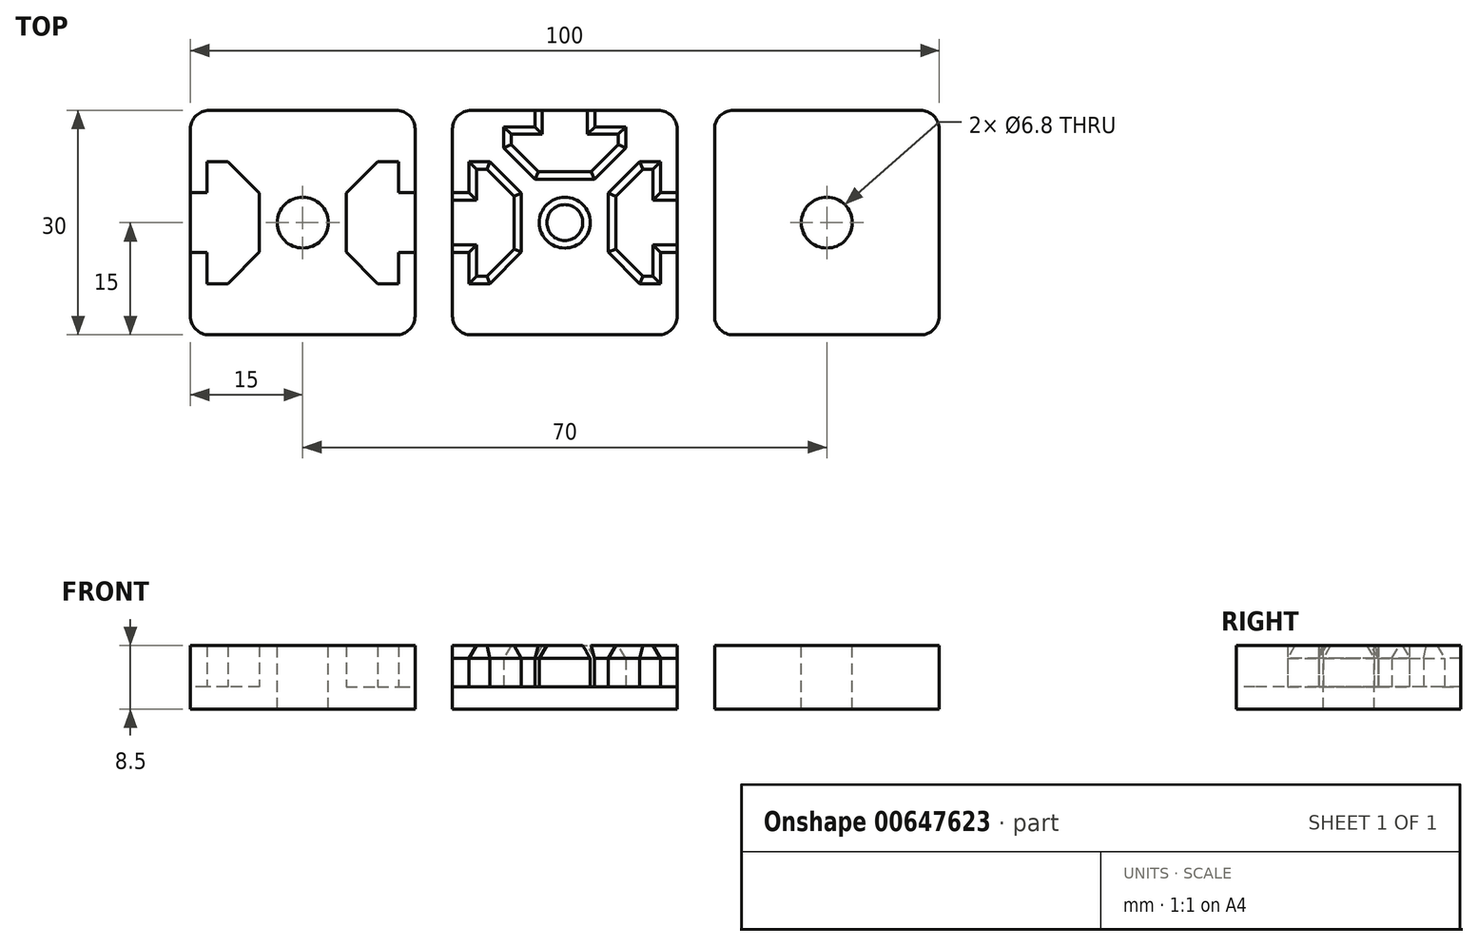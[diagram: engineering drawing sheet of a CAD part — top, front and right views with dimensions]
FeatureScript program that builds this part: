
annotation { "Feature Type Name" : "Feature", "Feature Type Description" : "" }
export const myFeature = defineFeature(function(context is Context, id is Id, definition is map)
    precondition{}
    {
        {
            var Q0;
            Q0=qCreatedBy(makeId("Top.planeOp"),FACE);
            var sketch = newSketch(context, id + "F0", { "sketchPlane" : qUnion([Q0])});
            skLineSegment(sketch, "E0.bottom", {"start": v(-12.5, 15) * mm, "end": v(12.5, 15) * mm});
            skLineSegment(sketch, "E0.top", {"start": v(-12.5, -15) * mm, "end": v(12.5, -15) * mm});
            skLineSegment(sketch, "E0.left", {"start": v(-15, 12.5) * mm, "end": v(-15, -12.5) * mm});
            skLineSegment(sketch, "E0.right", {"start": v(15, 12.5) * mm, "end": v(15, -12.5) * mm});
            skPoint(sketch, "E0.middle", {"position": v(0, 0) * mm});
            skPoint(sketch, "E1.visualSharp", {"position": v(-15, 15) * mm});
            skArc(sketch, "E1.filletArc", {"start": v(-12.5, 15) * mm, "mid": v(-14.27, 14.27) * mm, "end": v(-15, 12.5) * mm});
            skPoint(sketch, "E2.visualSharp", {"position": v(-15, -15) * mm});
            skArc(sketch, "E2.filletArc", {"start": v(-15, -12.5) * mm, "mid": v(-14.27, -14.27) * mm, "end": v(-12.5, -15) * mm});
            skPoint(sketch, "E3.visualSharp", {"position": v(15, -15) * mm});
            skArc(sketch, "E3.filletArc", {"start": v(12.5, -15) * mm, "mid": v(14.27, -14.27) * mm, "end": v(15, -12.5) * mm});
            skPoint(sketch, "E4.visualSharp", {"position": v(15, 15) * mm});
            skArc(sketch, "E4.filletArc", {"start": v(15, 12.5) * mm, "mid": v(14.27, 14.27) * mm, "end": v(12.5, 15) * mm});
            skLineSegment(sketch, "E5", {"start": v(-15, 15) * mm, "end": v(15, -15) * mm, "construction": true});
            skLineSegment(sketch, "E6", {"start": v(15, 15) * mm, "end": v(-15, -15) * mm, "construction": true});
            skLineSegment(sketch, "E7", {"start": v(15, 4) * mm, "end": v(12.8, 4) * mm});
            skLineSegment(sketch, "E8", {"start": v(12.8, 4) * mm, "end": v(12.8, 8.15) * mm});
            skLineSegment(sketch, "E9", {"start": v(12.8, 8.15) * mm, "end": v(10, 8.15) * mm});
            skLineSegment(sketch, "E10", {"start": v(10, 8.15) * mm, "end": v(5.8, 3.95) * mm});
            skLineSegment(sketch, "E11", {"start": v(5.8, 3.95) * mm, "end": v(5.8, -3.95) * mm});
            skLineSegment(sketch, "E12", {"start": v(5.8, -3.95) * mm, "end": v(10, -8.15) * mm});
            skLineSegment(sketch, "E13", {"start": v(10, -8.15) * mm, "end": v(12.8, -8.15) * mm});
            skLineSegment(sketch, "E14", {"start": v(12.8, -8.15) * mm, "end": v(12.8, -4) * mm});
            skLineSegment(sketch, "E15", {"start": v(12.8, -4) * mm, "end": v(15, -4) * mm});
            skPoint(sketch, "E16", {"position": v(5.8, 0) * mm});
            skLineSegment(sketch, "E17", {"start": v(12.8, 4) * mm, "end": v(12.8, -4) * mm, "construction": true});
            skPoint(sketch, "E18", {"position": v(12.8, 0) * mm});
            skLineSegment(sketch, "E19.MirrorCS", {"start": v(8.15, 10) * mm, "end": v(3.95, 5.8) * mm});
            skLineSegment(sketch, "E20.MirrorCS", {"start": v(8.15, 12.8) * mm, "end": v(8.15, 10) * mm});
            skLineSegment(sketch, "E21.MirrorCS", {"start": v(4, 12.8) * mm, "end": v(8.15, 12.8) * mm});
            skLineSegment(sketch, "E22.MirrorCS", {"start": v(4, 15) * mm, "end": v(4, 12.8) * mm});
            skLineSegment(sketch, "E23.MirrorCS", {"start": v(-4, 12.8) * mm, "end": v(-4, 15) * mm});
            skLineSegment(sketch, "E24.MirrorCS", {"start": v(-8.15, 12.8) * mm, "end": v(-4, 12.8) * mm});
            skLineSegment(sketch, "E25.MirrorCS", {"start": v(-8.15, 10) * mm, "end": v(-8.15, 12.8) * mm});
            skLineSegment(sketch, "E26.MirrorCS", {"start": v(-3.95, 5.8) * mm, "end": v(-8.15, 10) * mm});
            skLineSegment(sketch, "E27.MirrorCS", {"start": v(3.95, 5.8) * mm, "end": v(-3.95, 5.8) * mm});
            skLineSegment(sketch, "E28.MirrorCS", {"start": v(-5.8, -3.95) * mm, "end": v(-5.8, 3.95) * mm});
            skLineSegment(sketch, "E29.MirrorCS", {"start": v(-10, -8.15) * mm, "end": v(-5.8, -3.95) * mm});
            skLineSegment(sketch, "E30.MirrorCS", {"start": v(-12.8, -8.15) * mm, "end": v(-10, -8.15) * mm});
            skLineSegment(sketch, "E31.MirrorCS", {"start": v(-12.8, -4) * mm, "end": v(-12.8, -8.15) * mm});
            skLineSegment(sketch, "E32.MirrorCS", {"start": v(-15, -4) * mm, "end": v(-12.8, -4) * mm});
            skLineSegment(sketch, "E33.MirrorCS", {"start": v(-12.8, 4) * mm, "end": v(-15, 4) * mm});
            skLineSegment(sketch, "E34.MirrorCS", {"start": v(-12.8, 8.15) * mm, "end": v(-12.8, 4) * mm});
            skLineSegment(sketch, "E35.MirrorCS", {"start": v(-10, 8.15) * mm, "end": v(-12.8, 8.15) * mm});
            skLineSegment(sketch, "E36.MirrorCS", {"start": v(-5.8, 3.95) * mm, "end": v(-10, 8.15) * mm});
            skLineSegment(sketch, "E37.MirrorCS", {"start": v(-3.95, -5.8) * mm, "end": v(3.95, -5.8) * mm});
            skLineSegment(sketch, "E38.MirrorCS", {"start": v(-8.15, -10) * mm, "end": v(-3.95, -5.8) * mm});
            skLineSegment(sketch, "E39.MirrorCS", {"start": v(-8.15, -12.8) * mm, "end": v(-8.15, -10) * mm});
            skLineSegment(sketch, "E40.MirrorCS", {"start": v(-4, -12.8) * mm, "end": v(-8.15, -12.8) * mm});
            skLineSegment(sketch, "E41.MirrorCS", {"start": v(-4, -15) * mm, "end": v(-4, -12.8) * mm});
            skLineSegment(sketch, "E42.MirrorCS", {"start": v(4, -12.8) * mm, "end": v(4, -15) * mm});
            skLineSegment(sketch, "E43.MirrorCS", {"start": v(8.15, -12.8) * mm, "end": v(4, -12.8) * mm});
            skLineSegment(sketch, "E44.MirrorCS", {"start": v(8.15, -10) * mm, "end": v(8.15, -12.8) * mm});
            skLineSegment(sketch, "E45.MirrorCS", {"start": v(3.95, -5.8) * mm, "end": v(8.15, -10) * mm});
            skLineSegment(sketch, "E46", {"start": v(-17.5, 20.45) * mm, "end": v(-17.5, -22.2) * mm, "construction": true});
            skLineSegment(sketch, "E47", {"start": v(17.5, 19.31) * mm, "end": v(17.5, -20.78) * mm, "construction": true});
            skArc(sketch, "E48.MirrorCS", {"start": v(-22.5, 15) * mm, "mid": v(-20.73, 14.27) * mm, "end": v(-20, 12.5) * mm});
            skArc(sketch, "E49.MirrorCS", {"start": v(-20, -12.5) * mm, "mid": v(-20.73, -14.27) * mm, "end": v(-22.5, -15) * mm});
            skLineSegment(sketch, "E50.MirrorCS", {"start": v(-39, -12.8) * mm, "end": v(-39, -15) * mm});
            skLineSegment(sketch, "E51.MirrorCS", {"start": v(-39, 15) * mm, "end": v(-39, 12.8) * mm});
            skArc(sketch, "E52.MirrorCS", {"start": v(-47.5, -15) * mm, "mid": v(-49.27, -14.27) * mm, "end": v(-50, -12.5) * mm});
            skArc(sketch, "E53.MirrorCS", {"start": v(-50, 12.5) * mm, "mid": v(-49.27, 14.27) * mm, "end": v(-47.5, 15) * mm});
            skLineSegment(sketch, "E54.MirrorCS", {"start": v(-20, -4) * mm, "end": v(-22.2, -4) * mm});
            skLineSegment(sketch, "E55.MirrorCS", {"start": v(-31, 12.8) * mm, "end": v(-31, 15) * mm});
            skLineSegment(sketch, "E56.MirrorCS", {"start": v(-22.2, 4) * mm, "end": v(-20, 4) * mm});
            skLineSegment(sketch, "E57.MirrorCS", {"start": v(-31, -15) * mm, "end": v(-31, -12.8) * mm});
            skLineSegment(sketch, "E58.MirrorCS", {"start": v(-22.2, 8.15) * mm, "end": v(-22.2, 4) * mm});
            skLineSegment(sketch, "E59.MirrorCS", {"start": v(-47.8, 4) * mm, "end": v(-47.8, -4) * mm, "construction": true});
            skLineSegment(sketch, "E60.MirrorCS", {"start": v(-45, 8.15) * mm, "end": v(-40.8, 3.95) * mm});
            skLineSegment(sketch, "E61.MirrorCS", {"start": v(-43.15, -10) * mm, "end": v(-43.15, -12.8) * mm});
            skLineSegment(sketch, "E62.MirrorCS", {"start": v(-25, 8.15) * mm, "end": v(-22.2, 8.15) * mm});
            skLineSegment(sketch, "E63.MirrorCS", {"start": v(-29.2, -3.95) * mm, "end": v(-29.2, 3.95) * mm});
            skLineSegment(sketch, "E64.MirrorCS", {"start": v(-43.15, 10) * mm, "end": v(-38.95, 5.8) * mm});
            skLineSegment(sketch, "E65.MirrorCS", {"start": v(-50, 12.5) * mm, "end": v(-50, -12.5) * mm});
            skPoint(sketch, "E66.MirrorP", {"position": v(-20, -15) * mm});
            skLineSegment(sketch, "E67.MirrorCS", {"start": v(-43.15, -12.8) * mm, "end": v(-39, -12.8) * mm});
            skLineSegment(sketch, "E68.MirrorCS", {"start": v(-38.95, 5.8) * mm, "end": v(-31.05, 5.8) * mm});
            skLineSegment(sketch, "E69.MirrorCS", {"start": v(-38.95, -5.8) * mm, "end": v(-43.15, -10) * mm});
            skLineSegment(sketch, "E70.MirrorCS", {"start": v(-25, -8.15) * mm, "end": v(-29.2, -3.95) * mm});
            skLineSegment(sketch, "E71.MirrorCS", {"start": v(-29.2, 3.95) * mm, "end": v(-25, 8.15) * mm});
            skLineSegment(sketch, "E72.MirrorCS", {"start": v(-43.15, 12.8) * mm, "end": v(-43.15, 10) * mm});
            skLineSegment(sketch, "E73.MirrorCS", {"start": v(-26.85, 12.8) * mm, "end": v(-31, 12.8) * mm});
            skLineSegment(sketch, "E74.MirrorCS", {"start": v(-22.2, -8.15) * mm, "end": v(-25, -8.15) * mm});
            skPoint(sketch, "E75.MirrorP", {"position": v(-50, -15) * mm});
            skLineSegment(sketch, "E76.MirrorCS", {"start": v(-31.05, 5.8) * mm, "end": v(-26.85, 10) * mm});
            skLineSegment(sketch, "E77.MirrorCS", {"start": v(-26.85, -10) * mm, "end": v(-31.05, -5.8) * mm});
            skLineSegment(sketch, "E78.MirrorCS", {"start": v(-40.8, 3.95) * mm, "end": v(-40.8, -3.95) * mm});
            skLineSegment(sketch, "E79.MirrorCS", {"start": v(-40.8, -3.95) * mm, "end": v(-45, -8.15) * mm});
            skLineSegment(sketch, "E80.MirrorCS", {"start": v(-22.5, 15) * mm, "end": v(-47.5, 15) * mm});
            skLineSegment(sketch, "E81.MirrorCS", {"start": v(-22.5, -15) * mm, "end": v(-47.5, -15) * mm});
            skLineSegment(sketch, "E82.MirrorCS", {"start": v(-20, 12.5) * mm, "end": v(-20, -12.5) * mm});
            skPoint(sketch, "E83.MirrorP", {"position": v(-40.8, 0) * mm});
            skLineSegment(sketch, "E84.MirrorCS", {"start": v(-22.2, -4) * mm, "end": v(-22.2, -8.15) * mm});
            skLineSegment(sketch, "E85.MirrorCS", {"start": v(-45, -8.15) * mm, "end": v(-47.8, -8.15) * mm});
            skPoint(sketch, "E86.MirrorP", {"position": v(-47.8, 0) * mm});
            skLineSegment(sketch, "E87.MirrorCS", {"start": v(-47.8, -8.15) * mm, "end": v(-47.8, -4) * mm});
            skLineSegment(sketch, "E88.MirrorCS", {"start": v(-31, -12.8) * mm, "end": v(-26.85, -12.8) * mm});
            skLineSegment(sketch, "E89.MirrorCS", {"start": v(-20, 15) * mm, "end": v(-50, -15) * mm, "construction": true});
            skPoint(sketch, "E90.MirrorP", {"position": v(-20, 15) * mm});
            skLineSegment(sketch, "E91.MirrorCS", {"start": v(-26.85, -12.8) * mm, "end": v(-26.85, -10) * mm});
            skLineSegment(sketch, "E92.MirrorCS", {"start": v(-47.8, 4) * mm, "end": v(-47.8, 8.15) * mm});
            skLineSegment(sketch, "E93.MirrorCS", {"start": v(-47.8, 8.15) * mm, "end": v(-45, 8.15) * mm});
            skLineSegment(sketch, "E94.MirrorCS", {"start": v(-50, 15) * mm, "end": v(-20, -15) * mm, "construction": true});
            skPoint(sketch, "E95.MirrorP", {"position": v(-35, 0) * mm});
            skLineSegment(sketch, "E96.MirrorCS", {"start": v(-47.8, -4) * mm, "end": v(-50, -4) * mm});
            skLineSegment(sketch, "E97.MirrorCS", {"start": v(-26.85, 10) * mm, "end": v(-26.85, 12.8) * mm});
            skPoint(sketch, "E98.MirrorP", {"position": v(-50, 15) * mm});
            skLineSegment(sketch, "E99.MirrorCS", {"start": v(-31.05, -5.8) * mm, "end": v(-38.95, -5.8) * mm});
            skLineSegment(sketch, "E100.MirrorCS", {"start": v(-39, 12.8) * mm, "end": v(-43.15, 12.8) * mm});
            skLineSegment(sketch, "E101.MirrorCS", {"start": v(-50, 4) * mm, "end": v(-47.8, 4) * mm});
            skArc(sketch, "E102.MirrorCS", {"start": v(50, -12.5) * mm, "mid": v(49.27, -14.27) * mm, "end": v(47.5, -15) * mm});
            skLineSegment(sketch, "E103.MirrorCS", {"start": v(39, -15) * mm, "end": v(39, -12.8) * mm});
            skArc(sketch, "E104.MirrorCS", {"start": v(20, 12.5) * mm, "mid": v(20.73, 14.27) * mm, "end": v(22.5, 15) * mm});
            skArc(sketch, "E105.MirrorCS", {"start": v(22.5, -15) * mm, "mid": v(20.73, -14.27) * mm, "end": v(20, -12.5) * mm});
            skArc(sketch, "E106.MirrorCS", {"start": v(47.5, 15) * mm, "mid": v(49.27, 14.27) * mm, "end": v(50, 12.5) * mm});
            skLineSegment(sketch, "E107.MirrorCS", {"start": v(47.8, 4) * mm, "end": v(50, 4) * mm});
            skLineSegment(sketch, "E108.MirrorCS", {"start": v(31, -12.8) * mm, "end": v(31, -15) * mm});
            skLineSegment(sketch, "E109.MirrorCS", {"start": v(50, -4) * mm, "end": v(47.8, -4) * mm});
            skLineSegment(sketch, "E110.MirrorCS", {"start": v(22.2, -4) * mm, "end": v(20, -4) * mm});
            skLineSegment(sketch, "E111.MirrorCS", {"start": v(39, -12.8) * mm, "end": v(43.15, -12.8) * mm});
            skLineSegment(sketch, "E112.MirrorCS", {"start": v(22.2, -8.15) * mm, "end": v(22.2, -4) * mm});
            skLineSegment(sketch, "E113.MirrorCS", {"start": v(39, 12.8) * mm, "end": v(39, 15) * mm});
            skLineSegment(sketch, "E114.MirrorCS", {"start": v(31, 12.8) * mm, "end": v(26.85, 12.8) * mm});
            skLineSegment(sketch, "E115.MirrorCS", {"start": v(38.95, -5.8) * mm, "end": v(31.05, -5.8) * mm});
            skLineSegment(sketch, "E116.MirrorCS", {"start": v(47.8, -8.15) * mm, "end": v(45, -8.15) * mm});
            skLineSegment(sketch, "E117.MirrorCS", {"start": v(26.85, 12.8) * mm, "end": v(26.85, 10) * mm});
            skLineSegment(sketch, "E118.MirrorCS", {"start": v(40.8, 3.95) * mm, "end": v(45, 8.15) * mm});
            skLineSegment(sketch, "E119.MirrorCS", {"start": v(45, -8.15) * mm, "end": v(40.8, -3.95) * mm});
            skLineSegment(sketch, "E120.MirrorCS", {"start": v(31.05, -5.8) * mm, "end": v(26.85, -10) * mm});
            skLineSegment(sketch, "E121.MirrorCS", {"start": v(31.05, 5.8) * mm, "end": v(38.95, 5.8) * mm});
            skPoint(sketch, "E122.MirrorP", {"position": v(20, -15) * mm});
            skLineSegment(sketch, "E123.MirrorCS", {"start": v(26.85, -12.8) * mm, "end": v(31, -12.8) * mm});
            skLineSegment(sketch, "E124.MirrorCS", {"start": v(26.85, 10) * mm, "end": v(31.05, 5.8) * mm});
            skLineSegment(sketch, "E125.MirrorCS", {"start": v(45, 8.15) * mm, "end": v(47.8, 8.15) * mm});
            skLineSegment(sketch, "E126.MirrorCS", {"start": v(40.8, -3.95) * mm, "end": v(40.8, 3.95) * mm});
            skLineSegment(sketch, "E127.MirrorCS", {"start": v(26.85, -10) * mm, "end": v(26.85, -12.8) * mm});
            skLineSegment(sketch, "E128.MirrorCS", {"start": v(20, 12.5) * mm, "end": v(20, -12.5) * mm});
            skLineSegment(sketch, "E129.MirrorCS", {"start": v(43.15, 10) * mm, "end": v(43.15, 12.8) * mm});
            skPoint(sketch, "E130.MirrorP", {"position": v(50, 15) * mm});
            skLineSegment(sketch, "E131.MirrorCS", {"start": v(47.8, 8.15) * mm, "end": v(47.8, 4) * mm});
            skLineSegment(sketch, "E132.MirrorCS", {"start": v(29.2, 3.95) * mm, "end": v(29.2, -3.95) * mm});
            skPoint(sketch, "E133.MirrorP", {"position": v(50, -15) * mm});
            skLineSegment(sketch, "E134.MirrorCS", {"start": v(43.15, -10) * mm, "end": v(38.95, -5.8) * mm});
            skLineSegment(sketch, "E135.MirrorCS", {"start": v(20, 15) * mm, "end": v(50, -15) * mm, "construction": true});
            skLineSegment(sketch, "E136.MirrorCS", {"start": v(43.15, 12.8) * mm, "end": v(39, 12.8) * mm});
            skLineSegment(sketch, "E137.MirrorCS", {"start": v(29.2, -3.95) * mm, "end": v(25, -8.15) * mm});
            skPoint(sketch, "E138.MirrorP", {"position": v(29.2, 0) * mm});
            skLineSegment(sketch, "E139.MirrorCS", {"start": v(25, -8.15) * mm, "end": v(22.2, -8.15) * mm});
            skLineSegment(sketch, "E140.MirrorCS", {"start": v(38.95, 5.8) * mm, "end": v(43.15, 10) * mm});
            skLineSegment(sketch, "E141.MirrorCS", {"start": v(43.15, -12.8) * mm, "end": v(43.15, -10) * mm});
            skPoint(sketch, "E142.MirrorP", {"position": v(35, 0) * mm});
            skPoint(sketch, "E143.MirrorP", {"position": v(22.2, 0) * mm});
            skPoint(sketch, "E144.MirrorP", {"position": v(20, 15) * mm});
            skLineSegment(sketch, "E145.MirrorCS", {"start": v(22.2, 8.15) * mm, "end": v(25, 8.15) * mm});
            skLineSegment(sketch, "E146.MirrorCS", {"start": v(20, 4) * mm, "end": v(22.2, 4) * mm});
            skLineSegment(sketch, "E147.MirrorCS", {"start": v(22.2, 4) * mm, "end": v(22.2, 8.15) * mm});
            skLineSegment(sketch, "E148.MirrorCS", {"start": v(31, 15) * mm, "end": v(31, 12.8) * mm});
            skLineSegment(sketch, "E149.MirrorCS", {"start": v(50, 15) * mm, "end": v(20, -15) * mm, "construction": true});
            skLineSegment(sketch, "E150.MirrorCS", {"start": v(47.8, -4) * mm, "end": v(47.8, -8.15) * mm});
            skLineSegment(sketch, "E151.MirrorCS", {"start": v(22.2, 4) * mm, "end": v(22.2, -4) * mm, "construction": true});
            skLineSegment(sketch, "E152.MirrorCS", {"start": v(47.5, -15) * mm, "end": v(22.5, -15) * mm});
            skLineSegment(sketch, "E153.MirrorCS", {"start": v(47.5, 15) * mm, "end": v(22.5, 15) * mm});
            skLineSegment(sketch, "E154.MirrorCS", {"start": v(25, 8.15) * mm, "end": v(29.2, 3.95) * mm});
            skLineSegment(sketch, "E155.MirrorCS", {"start": v(50, 12.5) * mm, "end": v(50, -12.5) * mm});
            skCircle(sketch, "E156", {"center": v(0, 0) * mm, "radius": 3.4 * mm});
            skCircle(sketch, "E157.MirrorC", {"center": v(-35, 0) * mm, "radius": 3.4 * mm});
            skCircle(sketch, "E158.MirrorC", {"center": v(35, 0) * mm, "radius": 3.4 * mm});
            skSolve(sketch);
        }
        {
            var Q0;
            Q0=makeQuery(id+"F0.imprint","IMPRINT",FACE,{"disambiguationData":[TD([[makeQuery(id+"F0.imprint","IMPRINT",EDGE,{"derivedFrom":sQuery(id+"F0.wireOp",EDGE,"E0.bottom")}),-1.0]])]});
            var Q1;
            {var subQ0=sQuery(id+"F0.wireOp",EDGE,"E7");Q1=makeQuery(id+"F0.imprint","IMPRINT",FACE,{"disambiguationData":[TD([[makeQuery(id+"F0.imprint","IMPRINT",EDGE,{"derivedFrom":subQ0}),1.0]])]});}
            var Q2;
            Q2=makeQuery(id+"F0.imprint","IMPRINT",FACE,{"disambiguationData":[TD([[makeQuery(id+"F0.imprint","IMPRINT",EDGE,{"derivedFrom":sQuery(id+"F0.wireOp",EDGE,"E28.MirrorCS")}),1.0]])]});
            var Q3;
            Q3=makeQuery(id+"F0.imprint","IMPRINT",FACE,{"disambiguationData":[TD([[makeQuery(id+"F0.imprint","IMPRINT",EDGE,{"derivedFrom":sQuery(id+"F0.wireOp",EDGE,"E37.MirrorCS")}),-1.0]])]});
            var Q4;
            Q4=makeQuery(id+"F0.imprint","IMPRINT",FACE,{"disambiguationData":[TD([[makeQuery(id+"F0.imprint","IMPRINT",EDGE,{"derivedFrom":sQuery(id+"F0.wireOp",EDGE,"E19.MirrorCS")}),-1.0]])]});
            var Q5;
            Q5=makeQuery(id+"F0.imprint","IMPRINT",FACE,{"disambiguationData":[TD([[makeQuery(id+"F0.imprint","IMPRINT",EDGE,{"derivedFrom":sQuery(id+"F0.wireOp",EDGE,"E156")}),1.0]])]});
            extrude(context, id + "F1", {"entities" : qUnion([Q0, Q1, Q2, Q3, Q4, Q5]), "oppositeDirection" : true, "depth" : 3 * mm, "offsetDistance" : 25 * mm});
        }
        {
            var Q0;
            Q0=makeQuery(id+"F0.imprint","IMPRINT",FACE,{"disambiguationData":[TD([[makeQuery(id+"F0.imprint","IMPRINT",EDGE,{"derivedFrom":sQuery(id+"F0.wireOp",EDGE,"E28.MirrorCS")}),1.0]])]});
            var Q1;
            Q1=makeQuery(id+"F0.imprint","IMPRINT",FACE,{"disambiguationData":[TD([[makeQuery(id+"F0.imprint","IMPRINT",EDGE,{"derivedFrom":sQuery(id+"F0.wireOp",EDGE,"E19.MirrorCS")}),-1.0]])]});
            var Q2;
            {var subQ0=sQuery(id+"F0.wireOp",EDGE,"E7");Q2=makeQuery(id+"F0.imprint","IMPRINT",FACE,{"disambiguationData":[TD([[makeQuery(id+"F0.imprint","IMPRINT",EDGE,{"derivedFrom":subQ0}),1.0]])]});}
            var Q3;
            Q3=makeQuery(id+"F0.imprint","IMPRINT",FACE,{"disambiguationData":[TD([[makeQuery(id+"F0.imprint","IMPRINT",EDGE,{"derivedFrom":sQuery(id+"F0.wireOp",EDGE,"E156")}),1.0]])]});
            extrude(context, id + "F2", {"entities" : qUnion([Q0, Q1, Q2, Q3]), "operationType" : NewBodyOperationType.ADD, "depth" : 5.5 * mm, "offsetDistance" : 25 * mm});
        }
        {
            var Q0;
            {var subQ3=sQuery(id+"F0.wireOp",EDGE,"E48.MirrorCS");Q0=makeQuery(id+"F0.imprint","IMPRINT",FACE,{"disambiguationData":[TD([[makeQuery(id+"F0.imprint","IMPRINT",EDGE,{"derivedFrom":subQ3}),-1.0]])]});}
            var Q1;
            {var subQ1=sQuery(id+"F0.wireOp",EDGE,"E50.MirrorCS");Q1=makeQuery(id+"F0.imprint","IMPRINT",FACE,{"disambiguationData":[TD([[makeQuery(id+"F0.imprint","IMPRINT",EDGE,{"derivedFrom":subQ1}),1.0]])]});}
            var Q2;
            {var subQ1=sQuery(id+"F0.wireOp",EDGE,"E54.MirrorCS");Q2=makeQuery(id+"F0.imprint","IMPRINT",FACE,{"disambiguationData":[TD([[makeQuery(id+"F0.imprint","IMPRINT",EDGE,{"derivedFrom":subQ1}),-1.0]])]});}
            var Q3;
            {var subQ1=sQuery(id+"F0.wireOp",EDGE,"E51.MirrorCS");Q3=makeQuery(id+"F0.imprint","IMPRINT",FACE,{"disambiguationData":[TD([[makeQuery(id+"F0.imprint","IMPRINT",EDGE,{"derivedFrom":subQ1}),1.0]])]});}
            var Q4;
            Q4=makeQuery(id+"F0.imprint","IMPRINT",FACE,{"disambiguationData":[TD([[makeQuery(id+"F0.imprint","IMPRINT",EDGE,{"derivedFrom":sQuery(id+"F0.wireOp",EDGE,"E60.MirrorCS")}),-1.0]])]});
            var Q5;
            Q5=makeQuery(id+"F0.imprint","IMPRINT",FACE,{"disambiguationData":[TD([[makeQuery(id+"F0.imprint","IMPRINT",EDGE,{"derivedFrom":sQuery(id+"F0.wireOp",EDGE,"E157.MirrorC")}),-1.0]])]});
            var Q6;
            Q6=makeQuery(id+"F1.opExtrude","CAP_FACE",FACE,{"disambiguationData":[OSD([sQuery(id+"F0.wireOp",EDGE,"E0.bottom"),sQuery(id+"F0.wireOp",EDGE,"E0.top"),sQuery(id+"F0.wireOp",EDGE,"E0.left"),sQuery(id+"F0.wireOp",EDGE,"E0.right"),sQuery(id+"F0.wireOp",EDGE,"E1.filletArc"),sQuery(id+"F0.wireOp",EDGE,"E2.filletArc"),sQuery(id+"F0.wireOp",EDGE,"E3.filletArc"),sQuery(id+"F0.wireOp",EDGE,"E4.filletArc")])],"isStart":false});
            extrude(context, id + "F3", {"entities" : qUnion([Q0, Q1, Q2, Q3, Q4, Q5]), "endBound" : BoundingType.UP_TO_SURFACE, "oppositeDirection" : true, "depth" : 5 * mm, "endBoundEntityFace" : qUnion([Q6]), "offsetDistance" : 25 * mm});
        }
        {
            var Q0;
            {var subQ1=sQuery(id+"F0.wireOp",EDGE,"E51.MirrorCS");Q0=makeQuery(id+"F0.imprint","IMPRINT",FACE,{"disambiguationData":[TD([[makeQuery(id+"F0.imprint","IMPRINT",EDGE,{"derivedFrom":subQ1}),1.0]])]});}
            var Q1;
            Q1=makeQuery(id+"F0.imprint","IMPRINT",FACE,{"disambiguationData":[TD([[makeQuery(id+"F0.imprint","IMPRINT",EDGE,{"derivedFrom":sQuery(id+"F0.wireOp",EDGE,"E157.MirrorC")}),-1.0]])]});
            var Q2;
            {var subQ1=sQuery(id+"F0.wireOp",EDGE,"E50.MirrorCS");Q2=makeQuery(id+"F0.imprint","IMPRINT",FACE,{"disambiguationData":[TD([[makeQuery(id+"F0.imprint","IMPRINT",EDGE,{"derivedFrom":subQ1}),1.0]])]});}
            var Q3;
            Q3=makeQuery(id+"F2.opExtrude","CAP_FACE",FACE,{"disambiguationData":[OSD([sQuery(id+"F0.wireOp",EDGE,"E0.bottom"),sQuery(id+"F0.wireOp",EDGE,"E19.MirrorCS"),sQuery(id+"F0.wireOp",EDGE,"E20.MirrorCS"),sQuery(id+"F0.wireOp",EDGE,"E21.MirrorCS"),sQuery(id+"F0.wireOp",EDGE,"E22.MirrorCS"),sQuery(id+"F0.wireOp",EDGE,"E23.MirrorCS"),sQuery(id+"F0.wireOp",EDGE,"E24.MirrorCS"),sQuery(id+"F0.wireOp",EDGE,"E25.MirrorCS"),sQuery(id+"F0.wireOp",EDGE,"E26.MirrorCS"),sQuery(id+"F0.wireOp",EDGE,"E27.MirrorCS")])],"isStart":false});
            extrude(context, id + "F4", {"entities" : qUnion([Q0, Q1, Q2]), "operationType" : NewBodyOperationType.ADD, "endBound" : BoundingType.UP_TO_SURFACE, "depth" : 25 * mm, "endBoundEntityFace" : qUnion([Q3]), "offsetDistance" : 25 * mm});
        }
        {
            var Q0;
            {var subQ6=sQuery(id+"F0.wireOp",EDGE,"E102.MirrorCS");Q0=makeQuery(id+"F0.imprint","IMPRINT",FACE,{"disambiguationData":[TD([[makeQuery(id+"F0.imprint","IMPRINT",EDGE,{"derivedFrom":subQ6}),-1.0]])]});}
            var Q1;
            {var subQ0=sQuery(id+"F0.wireOp",EDGE,"E113.MirrorCS");Q1=makeQuery(id+"F0.imprint","IMPRINT",FACE,{"disambiguationData":[TD([[makeQuery(id+"F0.imprint","IMPRINT",EDGE,{"derivedFrom":subQ0}),1.0]])]});}
            var Q2;
            {var subQ1=sQuery(id+"F0.wireOp",EDGE,"E110.MirrorCS");Q2=makeQuery(id+"F0.imprint","IMPRINT",FACE,{"disambiguationData":[TD([[makeQuery(id+"F0.imprint","IMPRINT",EDGE,{"derivedFrom":subQ1}),-1.0]])]});}
            var Q3;
            {var subQ1=sQuery(id+"F0.wireOp",EDGE,"E103.MirrorCS");Q3=makeQuery(id+"F0.imprint","IMPRINT",FACE,{"disambiguationData":[TD([[makeQuery(id+"F0.imprint","IMPRINT",EDGE,{"derivedFrom":subQ1}),1.0]])]});}
            var Q4;
            {var subQ0=sQuery(id+"F0.wireOp",EDGE,"E107.MirrorCS");Q4=makeQuery(id+"F0.imprint","IMPRINT",FACE,{"disambiguationData":[TD([[makeQuery(id+"F0.imprint","IMPRINT",EDGE,{"derivedFrom":subQ0}),-1.0]])]});}
            var Q5;
            Q5=makeQuery(id+"F0.imprint","IMPRINT",FACE,{"disambiguationData":[TD([[makeQuery(id+"F0.imprint","IMPRINT",EDGE,{"derivedFrom":sQuery(id+"F0.wireOp",EDGE,"E158.MirrorC")}),-1.0]])]});
            var Q6;
            Q6=makeQuery(id+"F1.opExtrude","CAP_FACE",FACE,{"disambiguationData":[OSD([sQuery(id+"F0.wireOp",EDGE,"E0.bottom"),sQuery(id+"F0.wireOp",EDGE,"E0.top"),sQuery(id+"F0.wireOp",EDGE,"E0.left"),sQuery(id+"F0.wireOp",EDGE,"E0.right"),sQuery(id+"F0.wireOp",EDGE,"E1.filletArc"),sQuery(id+"F0.wireOp",EDGE,"E2.filletArc"),sQuery(id+"F0.wireOp",EDGE,"E3.filletArc"),sQuery(id+"F0.wireOp",EDGE,"E4.filletArc")])],"isStart":false});
            extrude(context, id + "F5", {"entities" : qUnion([Q0, Q1, Q2, Q3, Q4, Q5]), "endBound" : BoundingType.UP_TO_SURFACE, "oppositeDirection" : true, "depth" : 25 * mm, "endBoundEntityFace" : qUnion([Q6]), "offsetDistance" : 25 * mm});
        }
        {
            var Q0;
            {var subQ1=sQuery(id+"F0.wireOp",EDGE,"E110.MirrorCS");Q0=makeQuery(id+"F0.imprint","IMPRINT",FACE,{"disambiguationData":[TD([[makeQuery(id+"F0.imprint","IMPRINT",EDGE,{"derivedFrom":subQ1}),-1.0]])]});}
            var Q1;
            {var subQ0=sQuery(id+"F0.wireOp",EDGE,"E113.MirrorCS");Q1=makeQuery(id+"F0.imprint","IMPRINT",FACE,{"disambiguationData":[TD([[makeQuery(id+"F0.imprint","IMPRINT",EDGE,{"derivedFrom":subQ0}),1.0]])]});}
            var Q2;
            {var subQ0=sQuery(id+"F0.wireOp",EDGE,"E107.MirrorCS");Q2=makeQuery(id+"F0.imprint","IMPRINT",FACE,{"disambiguationData":[TD([[makeQuery(id+"F0.imprint","IMPRINT",EDGE,{"derivedFrom":subQ0}),-1.0]])]});}
            var Q3;
            {var subQ1=sQuery(id+"F0.wireOp",EDGE,"E103.MirrorCS");Q3=makeQuery(id+"F0.imprint","IMPRINT",FACE,{"disambiguationData":[TD([[makeQuery(id+"F0.imprint","IMPRINT",EDGE,{"derivedFrom":subQ1}),1.0]])]});}
            var Q4;
            Q4=makeQuery(id+"F0.imprint","IMPRINT",FACE,{"disambiguationData":[TD([[makeQuery(id+"F0.imprint","IMPRINT",EDGE,{"derivedFrom":sQuery(id+"F0.wireOp",EDGE,"E158.MirrorC")}),-1.0]])]});
            var Q5;
            Q5=makeQuery(id+"F2.opExtrude","CAP_FACE",FACE,{"disambiguationData":[OSD([sQuery(id+"F0.wireOp",EDGE,"E0.bottom"),sQuery(id+"F0.wireOp",EDGE,"E19.MirrorCS"),sQuery(id+"F0.wireOp",EDGE,"E20.MirrorCS"),sQuery(id+"F0.wireOp",EDGE,"E21.MirrorCS"),sQuery(id+"F0.wireOp",EDGE,"E22.MirrorCS"),sQuery(id+"F0.wireOp",EDGE,"E23.MirrorCS"),sQuery(id+"F0.wireOp",EDGE,"E24.MirrorCS"),sQuery(id+"F0.wireOp",EDGE,"E25.MirrorCS"),sQuery(id+"F0.wireOp",EDGE,"E26.MirrorCS"),sQuery(id+"F0.wireOp",EDGE,"E27.MirrorCS")])],"isStart":false});
            extrude(context, id + "F6", {"entities" : qUnion([Q0, Q1, Q2, Q3, Q4]), "operationType" : NewBodyOperationType.ADD, "endBound" : BoundingType.UP_TO_SURFACE, "depth" : 25 * mm, "endBoundEntityFace" : qUnion([Q5]), "offsetDistance" : 25 * mm});
        }
        {
            var Q0;
            Q0=makeQuery(id+"F2.opExtrude","CAP_EDGE",EDGE,{"disambiguationData":[OSD([sQuery(id+"F0.wireOp",EDGE,"E29.MirrorCS")])],"isStart":false});
            var Q1;
            Q1=makeQuery(id+"F2.opExtrude","CAP_EDGE",EDGE,{"disambiguationData":[OSD([sQuery(id+"F0.wireOp",EDGE,"E28.MirrorCS")])],"isStart":false});
            var Q2;
            Q2=makeQuery(id+"F2.opExtrude","CAP_EDGE",EDGE,{"disambiguationData":[OSD([sQuery(id+"F0.wireOp",EDGE,"E36.MirrorCS")])],"isStart":false});
            var Q3;
            Q3=makeQuery(id+"F2.opExtrude","CAP_EDGE",EDGE,{"disambiguationData":[OSD([sQuery(id+"F0.wireOp",EDGE,"E35.MirrorCS")])],"isStart":false});
            var Q4;
            Q4=makeQuery(id+"F2.opExtrude","CAP_EDGE",EDGE,{"disambiguationData":[OSD([sQuery(id+"F0.wireOp",EDGE,"E34.MirrorCS")])],"isStart":false});
            var Q5;
            Q5=makeQuery(id+"F2.opExtrude","CAP_EDGE",EDGE,{"disambiguationData":[OSD([sQuery(id+"F0.wireOp",EDGE,"E33.MirrorCS")])],"isStart":false});
            var Q6;
            Q6=makeQuery(id+"F2.opExtrude","CAP_EDGE",EDGE,{"disambiguationData":[OSD([sQuery(id+"F0.wireOp",EDGE,"E32.MirrorCS")])],"isStart":false});
            var Q7;
            Q7=makeQuery(id+"F2.opExtrude","CAP_EDGE",EDGE,{"disambiguationData":[OSD([sQuery(id+"F0.wireOp",EDGE,"E31.MirrorCS")])],"isStart":false});
            var Q8;
            Q8=makeQuery(id+"F2.opExtrude","CAP_EDGE",EDGE,{"disambiguationData":[OSD([sQuery(id+"F0.wireOp",EDGE,"E30.MirrorCS")])],"isStart":false});
            var Q9;
            Q9=makeQuery(id+"F2.opExtrude","CAP_EDGE",EDGE,{"disambiguationData":[OSD([sQuery(id+"F0.wireOp",EDGE,"E156")])],"isStart":false});
            var Q10;
            Q10=makeQuery(id+"F2.opExtrude","CAP_EDGE",EDGE,{"disambiguationData":[OSD([sQuery(id+"F0.wireOp",EDGE,"E15")])],"isStart":false});
            var Q11;
            Q11=makeQuery(id+"F2.opExtrude","CAP_EDGE",EDGE,{"disambiguationData":[OSD([sQuery(id+"F0.wireOp",EDGE,"E14")])],"isStart":false});
            var Q12;
            Q12=makeQuery(id+"F2.opExtrude","CAP_EDGE",EDGE,{"disambiguationData":[OSD([sQuery(id+"F0.wireOp",EDGE,"E13")])],"isStart":false});
            var Q13;
            Q13=makeQuery(id+"F2.opExtrude","CAP_EDGE",EDGE,{"disambiguationData":[OSD([sQuery(id+"F0.wireOp",EDGE,"E12")])],"isStart":false});
            var Q14;
            Q14=makeQuery(id+"F2.opExtrude","CAP_EDGE",EDGE,{"disambiguationData":[OSD([sQuery(id+"F0.wireOp",EDGE,"E11")])],"isStart":false});
            var Q15;
            Q15=makeQuery(id+"F2.opExtrude","CAP_EDGE",EDGE,{"disambiguationData":[OSD([sQuery(id+"F0.wireOp",EDGE,"E10")])],"isStart":false});
            var Q16;
            Q16=makeQuery(id+"F2.opExtrude","CAP_EDGE",EDGE,{"disambiguationData":[OSD([sQuery(id+"F0.wireOp",EDGE,"E9")])],"isStart":false});
            var Q17;
            Q17=makeQuery(id+"F2.opExtrude","CAP_EDGE",EDGE,{"disambiguationData":[OSD([sQuery(id+"F0.wireOp",EDGE,"E8")])],"isStart":false});
            var Q18;
            Q18=makeQuery(id+"F2.opExtrude","CAP_EDGE",EDGE,{"disambiguationData":[OSD([sQuery(id+"F0.wireOp",EDGE,"E7")])],"isStart":false});
            chamfer(context, id + "F7", {"entities" : qUnion([Q0, Q1, Q2, Q3, Q4, Q5, Q6, Q7, Q8, Q9, Q10, Q11, Q12, Q13, Q14, Q15, Q16, Q17, Q18]), "chamferType" : ChamferType.OFFSET_ANGLE, "width" : 1 * mm, "oppositeDirection" : false, "angle" : 60 * degree, "tangentPropagation" : true});
        }
        {
            var Q0;
            Q0=makeQuery(id+"F2.opExtrude","CAP_EDGE",EDGE,{"disambiguationData":[OSD([sQuery(id+"F0.wireOp",EDGE,"E25.MirrorCS")])],"isStart":false});
            var Q1;
            Q1=makeQuery(id+"F2.opExtrude","CAP_EDGE",EDGE,{"disambiguationData":[OSD([sQuery(id+"F0.wireOp",EDGE,"E26.MirrorCS")])],"isStart":false});
            var Q2;
            Q2=makeQuery(id+"F2.opExtrude","CAP_EDGE",EDGE,{"disambiguationData":[OSD([sQuery(id+"F0.wireOp",EDGE,"E27.MirrorCS")])],"isStart":false});
            var Q3;
            Q3=makeQuery(id+"F2.opExtrude","CAP_EDGE",EDGE,{"disambiguationData":[OSD([sQuery(id+"F0.wireOp",EDGE,"E19.MirrorCS")])],"isStart":false});
            var Q4;
            Q4=makeQuery(id+"F2.opExtrude","CAP_EDGE",EDGE,{"disambiguationData":[OSD([sQuery(id+"F0.wireOp",EDGE,"E20.MirrorCS")])],"isStart":false});
            var Q5;
            Q5=makeQuery(id+"F2.opExtrude","CAP_EDGE",EDGE,{"disambiguationData":[OSD([sQuery(id+"F0.wireOp",EDGE,"E21.MirrorCS")])],"isStart":false});
            var Q6;
            Q6=makeQuery(id+"F2.opExtrude","CAP_EDGE",EDGE,{"disambiguationData":[OSD([sQuery(id+"F0.wireOp",EDGE,"E24.MirrorCS")])],"isStart":false});
            var Q7;
            Q7=makeQuery(id+"F2.opExtrude","CAP_EDGE",EDGE,{"disambiguationData":[OSD([sQuery(id+"F0.wireOp",EDGE,"E23.MirrorCS")])],"isStart":false});
            var Q8;
            Q8=makeQuery(id+"F2.opExtrude","CAP_EDGE",EDGE,{"disambiguationData":[OSD([sQuery(id+"F0.wireOp",EDGE,"E22.MirrorCS")])],"isStart":false});
            chamfer(context, id + "F8", {"entities" : qUnion([Q0, Q1, Q2, Q3, Q4, Q5, Q6, Q7, Q8]), "chamferType" : ChamferType.OFFSET_ANGLE, "width" : 1 * mm, "oppositeDirection" : true, "angle" : 60 * degree, "tangentPropagation" : true});
        }
    });
